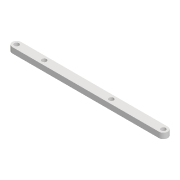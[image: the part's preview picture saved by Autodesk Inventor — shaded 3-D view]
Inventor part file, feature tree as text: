
AUTODESK INVENTOR PART (.ipt)
format: ipt  version: 2022 (Build 260153000, 153)  size: 96,768 bytes
history: native  units: mm
features: extrude x1
ambient origin geometry x8: Origin, YZ Plane, XZ Plane, XY Plane, X Axis, Y Axis, Z Axis, Center Point
bodies: Solid1 (feature_tree)
feature tree (1):
  extrude  "Extrusion1"  Depth=132.801mm
